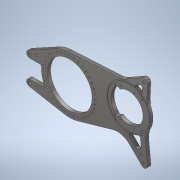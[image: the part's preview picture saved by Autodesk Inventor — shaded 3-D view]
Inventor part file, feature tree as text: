
AUTODESK INVENTOR PART (.ipt)
format: ipt  version: 2021 (Build 250183000, 183)  size: 592,384 bytes
history: native  units: in
note: dims shown in document units (in); Inventor stores cm internally (conversion verified against a paired STEP export)
features: sketch x19, extrude x13, hole x5, projected_geometry x3, chamfer x1, fillet x1
ambient origin geometry x8: Origin, YZ Plane, XZ Plane, XY Plane, X Axis, Y Axis, Z Axis, Center Point
bodies: Body1 (feature_tree)
feature tree (42):
  extrude  "Extrusion24"  Depth=2.16in
  extrude  "Extrusion28"  Depth=9.0in
  hole  "Hole9"  [1 undecoded]
  hole  "Hole11"  [1 undecoded]
  hole  "Hole13"  [1 undecoded]
  hole  "Hole14"  [1 undecoded]
  extrude  "Extrusion30"  Depth=0.5in
  extrude  "Extrusion31"  Depth=0.25in
  extrude  "Extrusion32"  Depth=7.75in
  extrude  "Extrusion33"  Depth=0.25in
  extrude  "Extrusion34"  Depth=1.0in
  chamfer  "Chamfer2"  Distance=5.0in
  extrude  "Extrusion35"  Depth=0.125in
  extrude  "Extrusion37"  Depth=0.125in TaperAngle=0.0deg
  extrude  "Extrusion39"  Depth=0.75in
  sketch  "Sketch58"  dims[d318=1.0in]
  hole  "Hole15"  [1 undecoded]
  extrude  "Extrusion40"  Depth=0.5in
  extrude  "Extrusion41"  Depth=0.75in
  fillet  "Fillet2"  Radius=0.75in
  extrude  "Extrusion42"  Depth=0.25in
  sketch  "Sketch2"  dims[d9=8.5in d92=2.16in]
  sketch  "Sketch35"  dims[d118=0.75in d119=0.75in d120=0.75in d121=0.75in d137=9.0in d142=6.5in]
  projected_geometry  "Projected Loop2"
  sketch  "Sketch36"  dims[d143=1.0in d210=1.0in]
  sketch  "Sketch40"  dims[d211=6.0in d212=6.0in]
  sketch  "Sketch43"  dims[d213=3.718in d214=1.0in]
  sketch  "Sketch45"  dims[d235=10.718in d237=1.5in]
  sketch  "Sketch46"  dims[d239=0.5in d240=0.0in d266=6.75in]
  sketch  "Sketch47"  dims[d267=0.5in d268=0.0in]
  sketch  "Sketch48"  dims[d269=0.386in d270=0.75in d271=0.762in d272=0.25in d273=0.5635in d274=0.484in d275=0.8108in d288=5.0in]
  sketch  "Sketch49"  dims[d289=17.223in d290=7.75in]
  sketch  "Sketch50"  dims[d291=3.5433in d293=360.0deg]
  sketch  "Sketch53"  dims[d295=0.257in d296=0.75in d297=0.438in d298=0.25in d299=0.5635in d300=1.0in d301=0.8108in d302=0.1718in]
  sketch  "Sketch55"  dims[d303=15.0deg d316=1.0in]
  sketch  "Sketch57"  dims[d317=0.0481in]
  sketch  "Sketch59"  dims[d319=0.3972in]
  sketch  "Sketch60"  dims[d322=0.271in]
  sketch  "Sketch62"  dims[d323=0.1355in]
  sketch  "Sketch63"  dims[d324=0.5in d325=0.266in d326=0.75in d327=0.507in d328=0.25in d329=0.5635in d330=1.0in d331=0.8108in d332=0.5in d333=0.5in d334=0.5in d335=0.5in d336=0.5in d337=3.0in d338=5.0in d339=0.196in d340=0.5in d341=0.507in d342=0.25in d343=0.5635in d344=0.75in d345=0.0in d346=3.0in d347=1.0in d348=0.0in d349=0.75in d350=0.75in d351=0.5in d353=0.75in d354=0.75in d355=0.25in d356=1.0in d357=0.0in d358=0.25in d359=1.0in d360=0.0in d361=1.0in d362=1.0in d363=0.25in d364=1.0in d365=0.0in d366=2.5in d367=1.0in d368=0.0in d373=0.0156in d374=0.125in d375=45.0deg d376=6.65in d377=6.25in d378=0.075in d379=0.0in d381=1.1915in d382=2.3407in d383=0.878in d384=2.3407in d395=0.5in d396=0.5in d397=1.0in d398=0.0in d403=1.0in d404=0.0in d405=0.5in d406=0.5in d407=2.01in d408=2.01in d409=2.01in d410=2.01in d411=2.01in d412=2.01in d413=2.01in d414=2.01in d415=0.196in d416=0.5in d417=0.375in d418=0.25in d419=0.5635in d420=1.0in d421=0.8108in d422=6.029in d423=6.63in d424=0.075in d425=0.0in d429=0.3369in d430=0.878in d431=2.1978in d432=1.0in d433=0.0in d434=0.125in d435=1.0in d436=0.0in]
  projected_geometry  "Project Cut Edges2"
  projected_geometry  "Project Cut Edges4"
note: 5 required parameter values undecoded (feature->parameter linkage not recoverable at this tier; creation-order binding heuristic only, values carry confidence <= 0.55)
